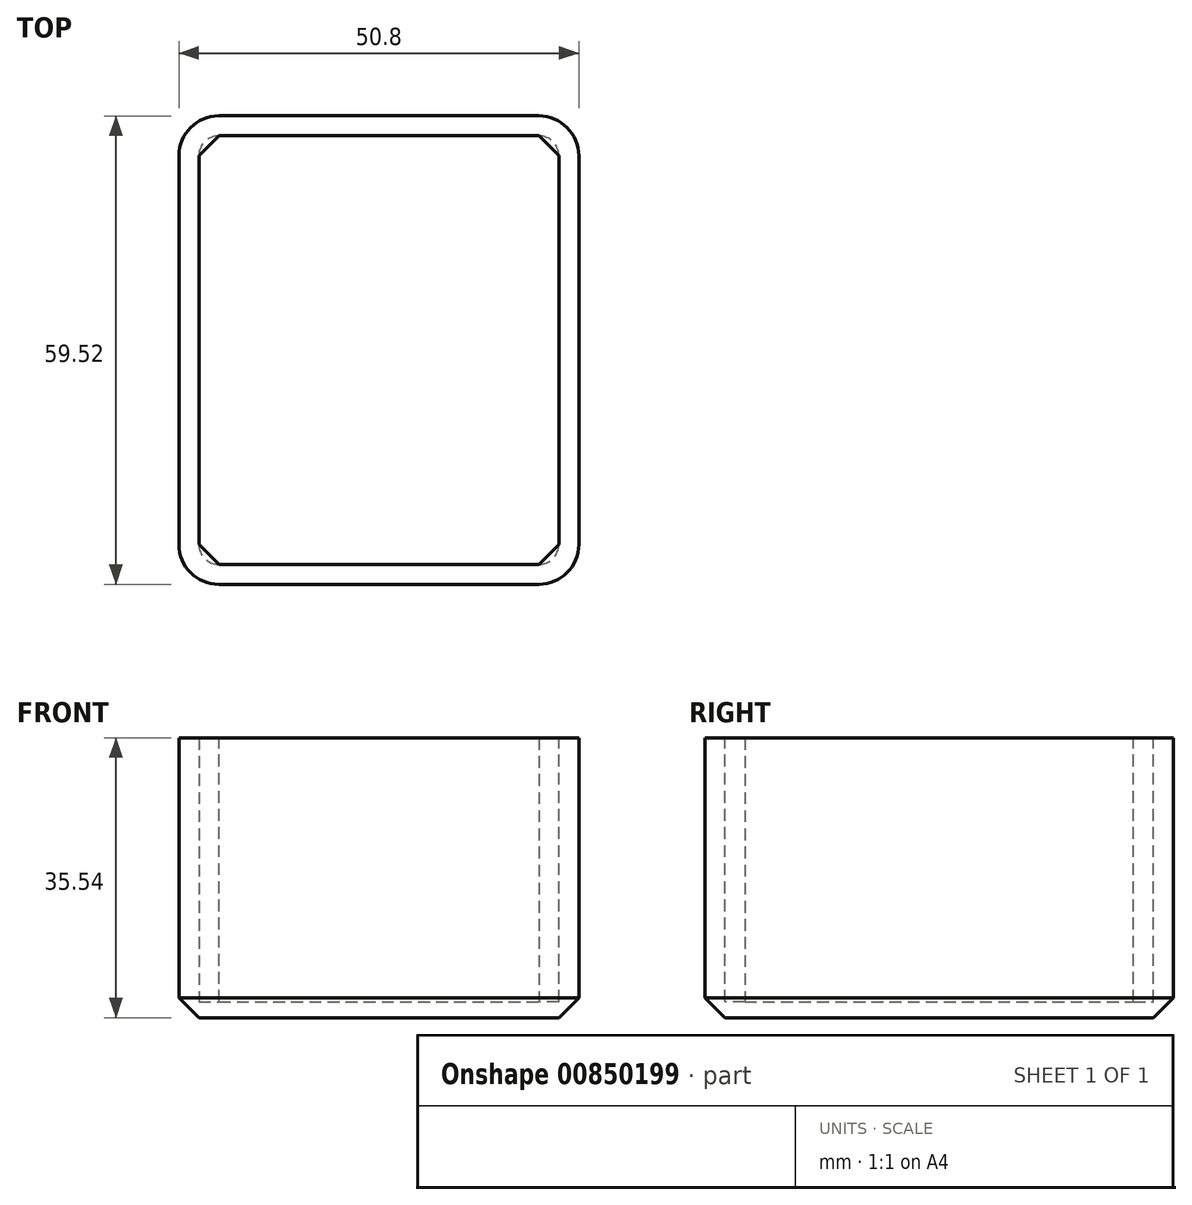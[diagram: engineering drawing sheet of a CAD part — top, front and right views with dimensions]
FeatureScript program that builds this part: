
annotation { "Feature Type Name" : "Feature", "Feature Type Description" : "" }
export const myFeature = defineFeature(function(context is Context, id is Id, definition is map)
    precondition{}
    {
        {
            var Q0;
            Q0=qCreatedBy(makeId("Right.planeOp"),FACE);
            var sketch = newSketch(context, id + "F0", { "sketchPlane" : qUnion([Q0])});
            skLineSegment(sketch, "E0.bottom", {"start": v(-29.86, 0) * mm, "end": v(29.66, 0) * mm});
            skLineSegment(sketch, "E0.top", {"start": v(-29.86, 35.54) * mm, "end": v(29.66, 35.54) * mm});
            skLineSegment(sketch, "E0.left", {"start": v(-29.86, 0) * mm, "end": v(-29.86, 35.54) * mm});
            skLineSegment(sketch, "E0.right", {"start": v(29.66, 0) * mm, "end": v(29.66, 35.54) * mm});
            skSolve(sketch);
        }
        {
            var Q0;
            Q0 = qSketchRegion(id + "F0", true);
            extrude(context, id + "F1", {"entities" : qUnion([Q0]), "depth" : 50.8 * mm, "offsetDistance" : 25.4 * mm});
        }
        {
            var Q0;
            Q0=makeQuery(id+"F1.opExtrude","SWEPT_FACE",FACE,{"disambiguationData":[OSD([sQuery(id+"F0.wireOp",EDGE,"E0.top")])]});
            var sketch = newSketch(context, id + "F2", { "sketchPlane" : qUnion([Q0])});
            skLineSegment(sketch, "E1.bottom", {"start": v(2.54, -27.32) * mm, "end": v(48.26, -27.32) * mm});
            skLineSegment(sketch, "E1.top", {"start": v(2.54, 27.12) * mm, "end": v(48.26, 27.12) * mm});
            skLineSegment(sketch, "E1.left", {"start": v(2.54, -27.32) * mm, "end": v(2.54, 27.12) * mm});
            skLineSegment(sketch, "E1.right", {"start": v(48.26, -27.32) * mm, "end": v(48.26, 27.12) * mm});
            skSolve(sketch);
        }
        {
            var Q0;
            Q0=makeQuery(id+"F2.imprint","IMPRINT",FACE,{"disambiguationData":[TD([[makeQuery(id+"F2.imprint","IMPRINT",EDGE,{"derivedFrom":sQuery(id+"F2.wireOp",EDGE,"E1.bottom")}),1.0]])]});
            extrude(context, id + "F3", {"entities" : qUnion([Q0]), "operationType" : NewBodyOperationType.REMOVE, "oppositeDirection" : true, "depth" : 33.53 * mm, "offsetDistance" : 25.4 * mm});
        }
        {
            var Q0;
            Q0=makeQuery(id+"F1.opExtrude","CAP_EDGE",EDGE,{"disambiguationData":[OSD([sQuery(id+"F0.wireOp",EDGE,"E0.right")])],"isStart":true});
            var Q1;
            Q1=makeQuery(id+"F1.opExtrude","CAP_EDGE",EDGE,{"disambiguationData":[OSD([sQuery(id+"F0.wireOp",EDGE,"E0.left")])],"isStart":true});
            fillet(context, id + "F4", {"entities" : qUnion([Q0, Q1]), "radius" : 5.08 * mm, "tangentPropagation" : true, "allowEdgeOverflow" : false});
        }
        {
            var Q0;
            Q0=makeQuery(id+"F1.opExtrude","CAP_EDGE",EDGE,{"disambiguationData":[OSD([sQuery(id+"F0.wireOp",EDGE,"E0.left")])],"isStart":false});
            fillet(context, id + "F5", {"entities" : qUnion([Q0]), "radius" : 5.08 * mm, "tangentPropagation" : true, "allowEdgeOverflow" : false});
        }
        {
            var Q0;
            Q0=makeQuery(id+"F1.opExtrude","CAP_EDGE",EDGE,{"disambiguationData":[OSD([sQuery(id+"F0.wireOp",EDGE,"E0.right")])],"isStart":false});
            fillet(context, id + "F6", {"entities" : qUnion([Q0]), "radius" : 5.08 * mm, "tangentPropagation" : true, "allowEdgeOverflow" : false});
        }
        {
            var Q0;
            Q0=makeQuery(id+"F3.boolean.opBoolean","COPY",EDGE,{"derivedFrom":makeQuery(id+"F3.opExtrude","SWEPT_EDGE",EDGE,{"disambiguationData":[OSD([sQuery(id+"F2.wireOp",EDGE,"E1.top"),sQuery(id+"F2.wireOp",EDGE,"E1.right")])]})});
            var Q1;
            Q1=makeQuery(id+"F3.boolean.opBoolean","COPY",EDGE,{"derivedFrom":makeQuery(id+"F3.opExtrude","SWEPT_EDGE",EDGE,{"disambiguationData":[OSD([sQuery(id+"F2.wireOp",EDGE,"E1.top"),sQuery(id+"F2.wireOp",EDGE,"E1.left")])]})});
            chamfer(context, id + "F7", {"entities" : qUnion([Q0, Q1]), "width" : 2.54 * mm, "tangentPropagation" : true});
        }
        {
            var Q0;
            Q0=makeQuery(id+"F3.boolean.opBoolean","COPY",EDGE,{"derivedFrom":makeQuery(id+"F3.opExtrude","SWEPT_EDGE",EDGE,{"disambiguationData":[OSD([sQuery(id+"F2.wireOp",EDGE,"E1.bottom"),sQuery(id+"F2.wireOp",EDGE,"E1.right")])]})});
            var Q1;
            Q1=makeQuery(id+"F3.boolean.opBoolean","COPY",EDGE,{"derivedFrom":makeQuery(id+"F3.opExtrude","SWEPT_EDGE",EDGE,{"disambiguationData":[OSD([sQuery(id+"F2.wireOp",EDGE,"E1.bottom"),sQuery(id+"F2.wireOp",EDGE,"E1.left")])]})});
            chamfer(context, id + "F8", {"entities" : qUnion([Q0, Q1]), "width" : 2.54 * mm, "tangentPropagation" : true});
        }
        {
            var Q0;
            Q0=makeQuery(id+"F1.opExtrude","SWEPT_FACE",FACE,{"disambiguationData":[OSD([sQuery(id+"F0.wireOp",EDGE,"E0.bottom")])]});
            chamfer(context, id + "F9", {"entities" : qUnion([Q0]), "width" : 2.54 * mm, "tangentPropagation" : true});
        }
    });
